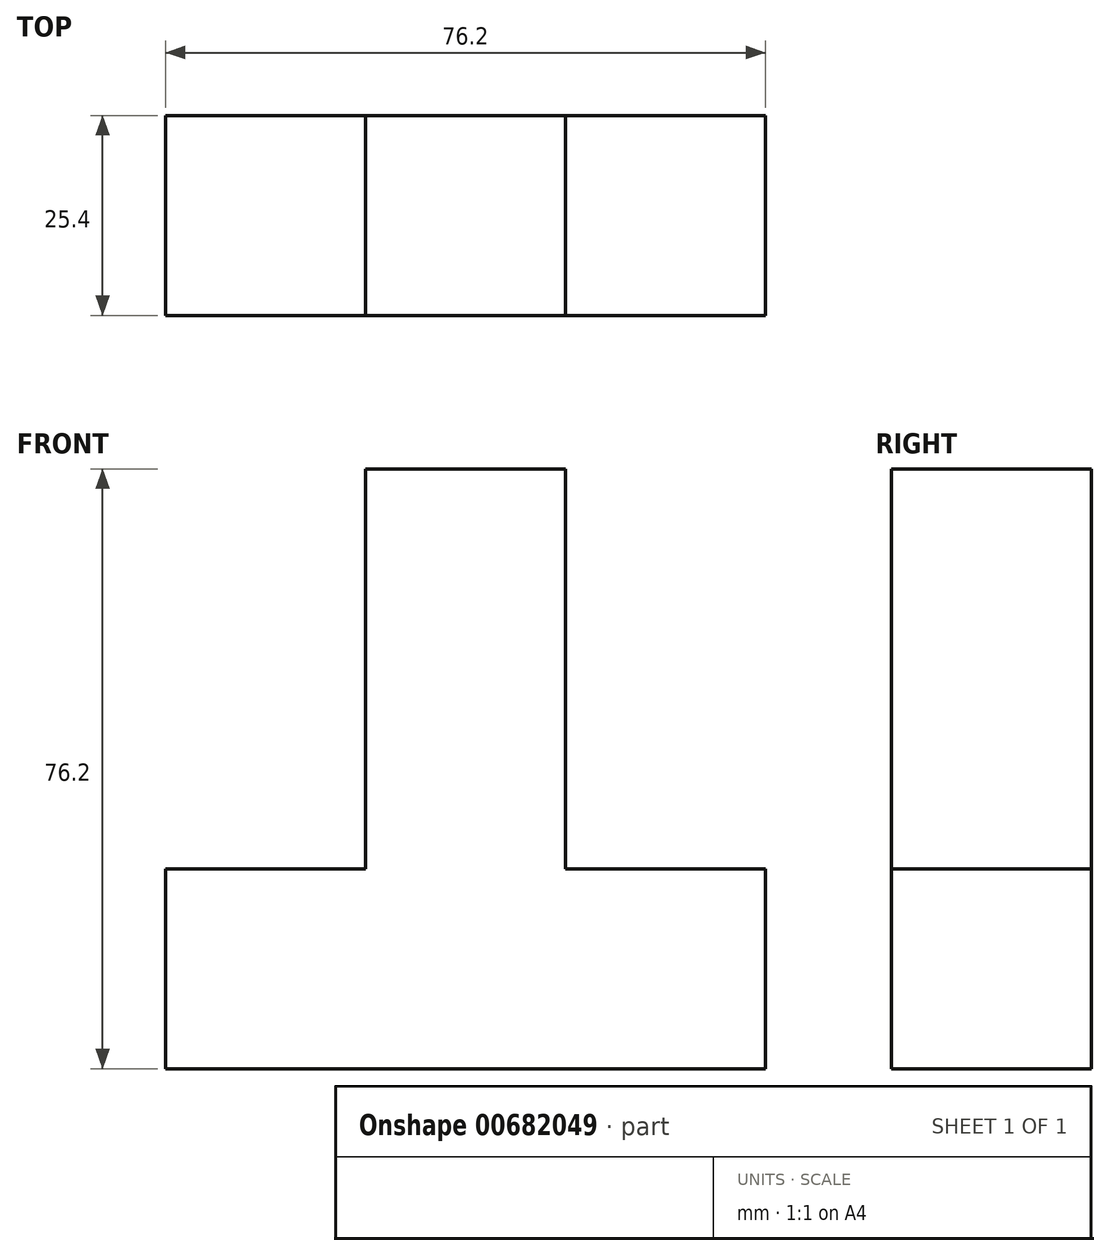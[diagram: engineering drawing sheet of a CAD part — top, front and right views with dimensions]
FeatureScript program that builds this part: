
annotation { "Feature Type Name" : "Feature", "Feature Type Description" : "" }
export const myFeature = defineFeature(function(context is Context, id is Id, definition is map)
    precondition{}
    {
        {
            var Q0;
            Q0=qCreatedBy(makeId("Front.planeOp"),FACE);
            var sketch = newSketch(context, id + "F0", { "sketchPlane" : qUnion([Q0])});
            skLineSegment(sketch, "E0", {"start": v(0, 0) * mm, "end": v(76.2, 0) * mm});
            skLineSegment(sketch, "E1", {"start": v(76.2, 0) * mm, "end": v(76.2, 25.4) * mm});
            skLineSegment(sketch, "E2", {"start": v(76.2, 25.4) * mm, "end": v(50.8, 25.4) * mm});
            skLineSegment(sketch, "E3", {"start": v(50.8, 25.4) * mm, "end": v(50.8, 76.2) * mm});
            skLineSegment(sketch, "E4", {"start": v(0, 0) * mm, "end": v(0, 25.4) * mm});
            skLineSegment(sketch, "E5", {"start": v(0, 25.4) * mm, "end": v(25.4, 25.4) * mm});
            skLineSegment(sketch, "E6", {"start": v(25.4, 25.4) * mm, "end": v(25.4, 76.2) * mm});
            skLineSegment(sketch, "E7", {"start": v(25.4, 76.2) * mm, "end": v(50.8, 76.2) * mm});
            skSolve(sketch);
        }
        {
            var Q0;
            Q0 = qSketchRegion(id + "F0", true);
            extrude(context, id + "F1", {"entities" : qUnion([Q0]), "depth" : 25.4 * mm, "offsetDistance" : 25.4 * mm});
        }
    });
